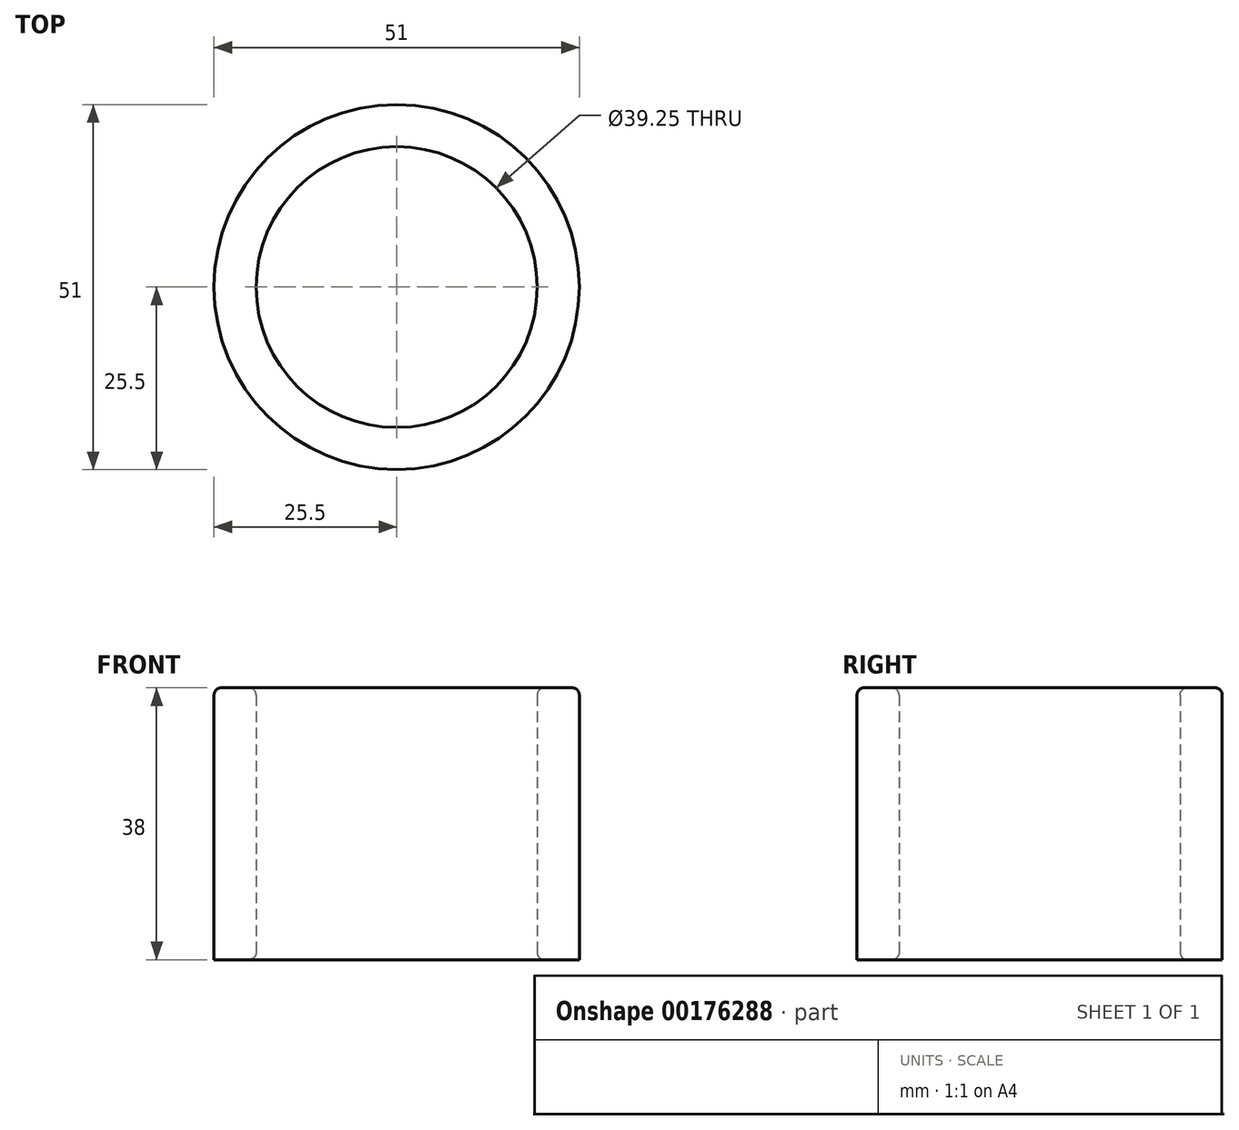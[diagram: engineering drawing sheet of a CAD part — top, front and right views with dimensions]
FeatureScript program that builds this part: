
annotation { "Feature Type Name" : "Feature", "Feature Type Description" : "" }
export const myFeature = defineFeature(function(context is Context, id is Id, definition is map)
    precondition{}
    {
        {
            var Q0;
            Q0=qCreatedBy(makeId("Top.planeOp"),FACE);
            var sketch = newSketch(context, id + "F0", { "sketchPlane" : qUnion([Q0])});
            skCircle(sketch, "E0", {"center": v(0, 0) * mm, "radius": 25.5 * mm});
            skCircle(sketch, "E1", {"center": v(0, 0) * mm, "radius": 19.62 * mm});
            skSolve(sketch);
        }
        {
            var Q0;
            Q0=makeQuery(id+"F0.imprint","IMPRINT",FACE,{"disambiguationData":[TD([[makeQuery(id+"F0.imprint","IMPRINT",EDGE,{"derivedFrom":sQuery(id+"F0.wireOp",EDGE,"E0")}),1.0]])]});
            extrude(context, id + "F1", {"entities" : qUnion([Q0]), "depth" : 38 * mm});
        }
        {
            var Q0;
            Q0=makeQuery(id+"F1.opExtrude","CAP_EDGE",EDGE,{"disambiguationData":[OSD([sQuery(id+"F0.wireOp",EDGE,"E1")])],"isStart":false});
            var Q1;
            Q1=makeQuery(id+"F1.opExtrude","CAP_EDGE",EDGE,{"disambiguationData":[OSD([sQuery(id+"F0.wireOp",EDGE,"E1")])],"isStart":true});
            var Q2;
            Q2=makeQuery(id+"F1.opExtrude","CAP_EDGE",EDGE,{"disambiguationData":[OSD([sQuery(id+"F0.wireOp",EDGE,"E0")])],"isStart":false});
            fillet(context, id + "F2", {"entities" : qUnion([Q0, Q1, Q2]), "radius" : 1 * mm, "tangentPropagation" : true, "allowEdgeOverflow" : false});
        }
    });
